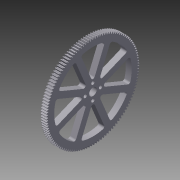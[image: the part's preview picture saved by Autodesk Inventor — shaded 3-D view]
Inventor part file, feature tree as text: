
AUTODESK INVENTOR PART (.ipt)
format: ipt  version: 2012 (Build 160160000, 160)  size: 808,960 bytes
history: native  units: in
note: dims shown in document units (in); Inventor stores cm internally (conversion verified against a paired STEP export)
features: imported_body x1, extrude x1, fillet x1, pattern_circular x1, sketch x1
ambient origin geometry x8: Origin, YZ Plane, XZ Plane, XY Plane, X Axis, Y Axis, Z Axis, Center Point
bodies: Solid1 (feature_tree)
feature tree (5):
  imported_body  "Base1"
  extrude  "Extrusion1"  Depth=0.0787in
  fillet  "Fillet1"  [1 undecoded]
  pattern_circular  "Circular Pattern1"  Angle=22.5deg  [1 undecoded]
  sketch  "Sketch1"  dims[d1=0.25in d10=0.0787in d11=22.5deg d12=22.5deg d13=0.6404in d14=0.3937in d15=0.0in d16=0.0787in d17=3.1496in d18=360.0deg]
note: 2 required parameter values undecoded (feature->parameter linkage not recoverable at this tier; creation-order binding heuristic only, values carry confidence <= 0.55)
